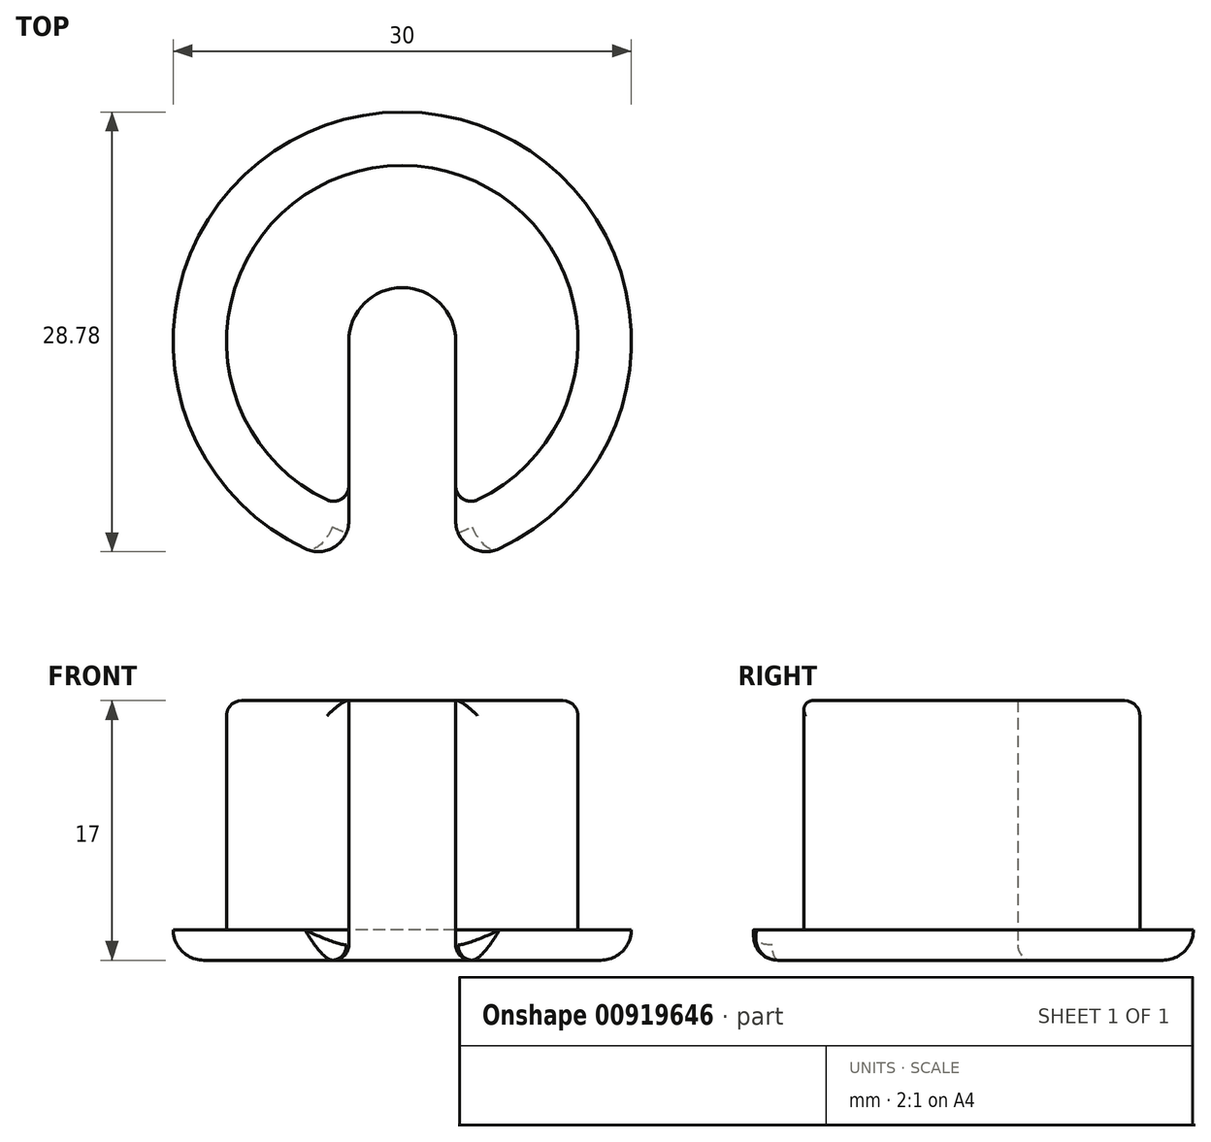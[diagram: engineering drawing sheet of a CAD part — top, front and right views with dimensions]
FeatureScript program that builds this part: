
annotation { "Feature Type Name" : "Feature", "Feature Type Description" : "" }
export const myFeature = defineFeature(function(context is Context, id is Id, definition is map)
    precondition{}
    {
        {
            var Q0;
            Q0=qCreatedBy(makeId("Top.planeOp"),FACE);
            var sketch = newSketch(context, id + "F0", { "sketchPlane" : qUnion([Q0])});
            skCircle(sketch, "E0", {"center": v(0, 0) * mm, "radius": 11.5 * mm});
            skCircle(sketch, "E1", {"center": v(0, 0) * mm, "radius": 15 * mm});
            skCircle(sketch, "E2", {"center": v(0, 0) * mm, "radius": 3.5 * mm});
            skLineSegment(sketch, "E3", {"start": v(0, 0) * mm, "end": v(3.5, 0) * mm});
            skLineSegment(sketch, "E4", {"start": v(3.5, 0) * mm, "end": v(3.5, -18) * mm});
            skLineSegment(sketch, "E5", {"start": v(3.5, -18) * mm, "end": v(-3.5, -18) * mm});
            skLineSegment(sketch, "E6", {"start": v(-3.5, -18) * mm, "end": v(-3.5, 0) * mm});
            skLineSegment(sketch, "E7", {"start": v(-3.5, 0) * mm, "end": v(0, 0) * mm});
            skSolve(sketch);
        }
        {
            var Q0;
            {var subQ0=sQuery(id+"F0.wireOp",EDGE,"E4");var subQ1=sQuery(id+"F0.wireOp",EDGE,"E0");var subQ2=makeQuery(id+"F0.imprint","INTERSECT",VERTEX,{"derivedFrom":[subQ1,subQ0]});Q0=makeQuery(id+"F0.imprint","IMPRINT",FACE,{"disambiguationData":[TD([[makeQuery(id+"F0.imprint","IMPRINT",EDGE,{"disambiguationData":[TD([[subQ2,-1.0]])],"derivedFrom":subQ1}),1.0]])]});}
            extrude(context, id + "F1", {"entities" : qUnion([Q0]), "depth" : 17 * mm, "offsetDistance" : 25 * mm});
        }
        {
            var Q0;
            {var subQ0=sQuery(id+"F0.wireOp",EDGE,"E4");var subQ1=sQuery(id+"F0.wireOp",EDGE,"E0");var subQ2=makeQuery(id+"F0.imprint","INTERSECT",VERTEX,{"derivedFrom":[subQ1,subQ0]});Q0=makeQuery(id+"F0.imprint","IMPRINT",FACE,{"disambiguationData":[TD([[makeQuery(id+"F0.imprint","IMPRINT",EDGE,{"disambiguationData":[TD([[subQ2,-1.0]])],"derivedFrom":subQ1}),-1.0]])]});}
            extrude(context, id + "F2", {"entities" : qUnion([Q0]), "operationType" : NewBodyOperationType.ADD, "depth" : 2 * mm, "offsetDistance" : 25 * mm});
        }
        {
            var Q0;
            Q0=makeQuery(id+"F1.opExtrude","CAP_EDGE",EDGE,{"disambiguationData":[OSD([sQuery(id+"F0.wireOp",EDGE,"E2")])],"isStart":true});
            var Q1;
            {var subQ0=sQuery(id+"F0.wireOp",EDGE,"E4");Q1=makeQuery(id+"F2.boolean.opBoolean","MERGE",EDGE,{"derivedFrom":[makeQuery(id+"F1.opExtrude","CAP_EDGE",EDGE,{"disambiguationData":[OSD([subQ0])],"isStart":true}),makeQuery(id+"F2.opExtrude","CAP_EDGE",EDGE,{"disambiguationData":[OSD([subQ0])],"isStart":true})]});}
            var Q2;
            Q2=makeQuery(id+"F1.opExtrude","SWEPT_EDGE",EDGE,{"disambiguationData":[OSD([sQuery(id+"F0.wireOp",EDGE,"E2"),sQuery(id+"F0.wireOp",EDGE,"E6")])]});
            var Q3;
            Q3=makeQuery(id+"F1.opExtrude","SWEPT_EDGE",EDGE,{"disambiguationData":[OSD([sQuery(id+"F0.wireOp",EDGE,"E0"),sQuery(id+"F0.wireOp",EDGE,"E4")])]});
            var Q4;
            Q4=makeQuery(id+"F1.opExtrude","SWEPT_EDGE",EDGE,{"disambiguationData":[OSD([sQuery(id+"F0.wireOp",EDGE,"E0"),sQuery(id+"F0.wireOp",EDGE,"E6")])]});
            var Q5;
            Q5=makeQuery(id+"F1.opExtrude","SWEPT_EDGE",EDGE,{"disambiguationData":[OSD([sQuery(id+"F0.wireOp",EDGE,"E2"),sQuery(id+"F0.wireOp",EDGE,"E4")])]});
            var Q6;
            {var subQ0=sQuery(id+"F0.wireOp",EDGE,"E6");Q6=makeQuery(id+"F2.boolean.opBoolean","MERGE",EDGE,{"derivedFrom":[makeQuery(id+"F1.opExtrude","CAP_EDGE",EDGE,{"disambiguationData":[OSD([subQ0])],"isStart":true}),makeQuery(id+"F2.opExtrude","CAP_EDGE",EDGE,{"disambiguationData":[OSD([subQ0])],"isStart":true})]});}
            var Q7;
            Q7=makeQuery(id+"F1.opExtrude","CAP_EDGE",EDGE,{"disambiguationData":[OSD([sQuery(id+"F0.wireOp",EDGE,"E0")])],"isStart":false});
            fillet(context, id + "F3", {"entities" : qUnion([Q0, Q1, Q2, Q3, Q4, Q5, Q6, Q7]), "radius" : 1 * mm, "tangentPropagation" : true, "allowEdgeOverflow" : false});
        }
        {
            var Q0;
            Q0=makeQuery(id+"F2.opExtrude","CAP_EDGE",EDGE,{"disambiguationData":[OSD([sQuery(id+"F0.wireOp",EDGE,"E1")])],"isStart":true});
            fillet(context, id + "F4", {"entities" : qUnion([Q0]), "radius" : 2 * mm, "tangentPropagation" : true, "allowEdgeOverflow" : false});
        }
    });
